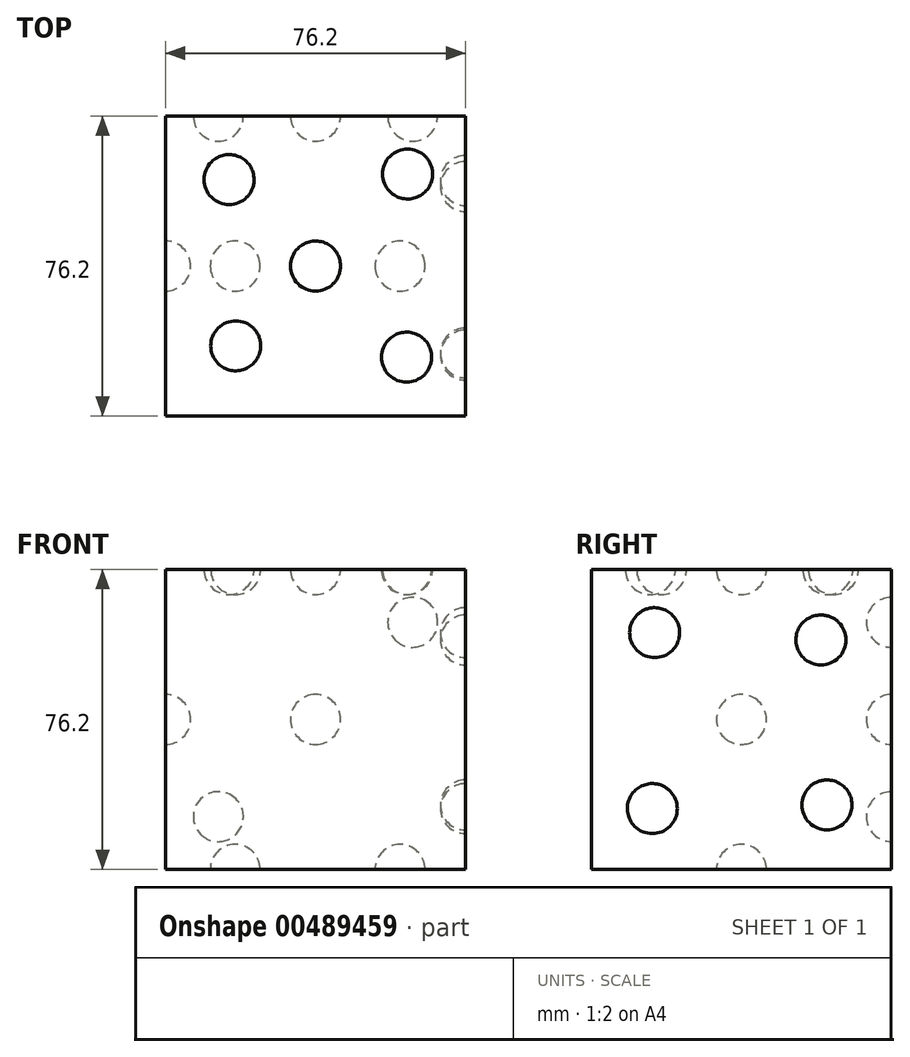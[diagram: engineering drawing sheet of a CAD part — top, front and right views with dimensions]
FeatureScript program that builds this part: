
annotation { "Feature Type Name" : "Feature", "Feature Type Description" : "" }
export const myFeature = defineFeature(function(context is Context, id is Id, definition is map)
    precondition{}
    {
        {
            var Q0;
            Q0=qCreatedBy(makeId("Top.planeOp"),FACE);
            var sketch = newSketch(context, id + "F0", { "sketchPlane" : qUnion([Q0])});
            skLineSegment(sketch, "E0", {"start": v(0, 0) * mm, "end": v(0, 76.2) * mm});
            skLineSegment(sketch, "E1", {"start": v(0, 76.2) * mm, "end": v(-76.2, 76.2) * mm});
            skLineSegment(sketch, "E2", {"start": v(-76.2, 76.2) * mm, "end": v(-76.2, 0) * mm});
            skLineSegment(sketch, "E3", {"start": v(-76.2, 0) * mm, "end": v(0, 0) * mm});
            skSolve(sketch);
        }
        {
            var Q0;
            Q0 = qSketchRegion(id + "F0", true);
            extrude(context, id + "F1", {"entities" : qUnion([Q0]), "depth" : 76.2 * mm});
        }
        {
            var Q0;
            Q0=qCreatedBy(makeId("Front.planeOp"),FACE);
            cPlane(context, id + "F2", {"entities" : qUnion([Q0]), "cplaneType" : CPlaneType.OFFSET, "offset" : 76.2 * mm, "oppositeDirection" : true, "width" : 152.4 * mm, "height" : 152.4 * mm});
        }
        {
            var Q0;
            Q0=qCreatedBy(id+"F2.planeOp",FACE);
            var sketch = newSketch(context, id + "F3", { "sketchPlane" : qUnion([Q0])});
            skPoint(sketch, "E4.trimOffspring.end.orphan", {"position": v(0, 0) * mm});
            skLineSegment(sketch, "E5", {"start": v(-76.2, 76.2) * mm, "end": v(-76.2, 0) * mm});
            skLineSegment(sketch, "E6", {"start": v(-76.2, 0) * mm, "end": v(0, 0) * mm});
            skLineSegment(sketch, "E7", {"start": v(0, 76.2) * mm, "end": v(-76.2, 76.2) * mm});
            skArc(sketch, "E8", {"start": v(-38.1, 31.75) * mm, "mid": v(-31.75, 38.1) * mm, "end": v(-38.1, 44.45) * mm});
            skLineSegment(sketch, "E9", {"start": v(-38.1, 76.2) * mm, "end": v(-38.1, 0) * mm});
            skSolve(sketch);
        }
        {
            var Q0;
            {var subQ0=sQuery(id+"F3.wireOp",EDGE,"E8");Q0=makeQuery(id+"F3.imprint","IMPRINT",FACE,{"disambiguationData":[TD([[makeQuery(id+"F3.imprint","IMPRINT",EDGE,{"derivedFrom":subQ0}),1.0]])]});}
            var Q1;
            Q1=sQuery(id+"F3.wireOp",EDGE,"E9");
            revolve(context, id + "F4", {"operationType" : NewBodyOperationType.REMOVE, "entities" : qUnion([Q0]), "axis" : qUnion([Q1]), "revolveType" : RevolveType.FULL});
        }
        {
            var Q0;
            Q0=makeQuery(id+"F1.opExtrude","SWEPT_FACE",FACE,{"disambiguationData":[OSD([sQuery(id+"F0.wireOp",EDGE,"E2")])]});
            var sketch = newSketch(context, id + "F5", { "sketchPlane" : qUnion([Q0])});
            skLineSegment(sketch, "E10", {"start": v(-76.2, 76.2) * mm, "end": v(0, 0) * mm});
            skArc(sketch, "E11", {"start": v(-42.6, 42.6) * mm, "mid": v(-42.6, 33.6) * mm, "end": v(-33.6, 33.6) * mm});
            skSolve(sketch);
        }
        {
            var Q0;
            {var subQ0=sQuery(id+"F5.wireOp",EDGE,"E11");Q0=makeQuery(id+"F5.imprint","IMPRINT",FACE,{"disambiguationData":[TD([[makeQuery(id+"F5.imprint","IMPRINT",EDGE,{"derivedFrom":subQ0}),1.0]])]});}
            var Q1;
            Q1=sQuery(id+"F5.wireOp",EDGE,"E10");
            revolve(context, id + "F6", {"operationType" : NewBodyOperationType.REMOVE, "entities" : qUnion([Q0]), "axis" : qUnion([Q1]), "revolveType" : RevolveType.FULL, "oppositeDirection" : true});
        }
        {
            var Q0;
            Q0=makeQuery(id+"F1.opExtrude","SWEPT_FACE",FACE,{"disambiguationData":[OSD([sQuery(id+"F0.wireOp",EDGE,"E1")])]});
            var sketch = newSketch(context, id + "F7", { "sketchPlane" : qUnion([Q0])});
            skLineSegment(sketch, "E12", {"start": v(0, 76.2) * mm, "end": v(76.2, 0) * mm});
            skArc(sketch, "E13", {"start": v(17.9, 58.3) * mm, "mid": v(17.9, 67.29) * mm, "end": v(8.91, 67.29) * mm});
            skArc(sketch, "E14", {"start": v(67.29, 8.91) * mm, "mid": v(67.29, 17.9) * mm, "end": v(58.3, 17.9) * mm});
            skSolve(sketch);
        }
        {
            var Q0;
            {var subQ0=sQuery(id+"F7.wireOp",EDGE,"E13");Q0=makeQuery(id+"F7.imprint","IMPRINT",FACE,{"disambiguationData":[TD([[makeQuery(id+"F7.imprint","IMPRINT",EDGE,{"derivedFrom":subQ0}),1.0]])]});}
            var Q1;
            {var subQ0=sQuery(id+"F7.wireOp",EDGE,"E14");Q1=makeQuery(id+"F7.imprint","IMPRINT",FACE,{"disambiguationData":[TD([[makeQuery(id+"F7.imprint","IMPRINT",EDGE,{"derivedFrom":subQ0}),1.0]])]});}
            var Q2;
            Q2=sQuery(id+"F7.wireOp",EDGE,"E12");
            revolve(context, id + "F8", {"operationType" : NewBodyOperationType.REMOVE, "entities" : qUnion([Q0, Q1]), "axis" : qUnion([Q2]), "revolveType" : RevolveType.FULL, "oppositeDirection" : true});
        }
        {
            var Q0;
            Q0=makeQuery(id+"F1.opExtrude","SWEPT_FACE",FACE,{"disambiguationData":[OSD([sQuery(id+"F0.wireOp",EDGE,"E0")])]});
            var sketch = newSketch(context, id + "F9", { "sketchPlane" : qUnion([Q0])});
            skLineSegment(sketch, "E15", {"start": v(0, 76.2) * mm, "end": v(76.2, 0) * mm});
            skArc(sketch, "E16", {"start": v(64.31, 11.89) * mm, "mid": v(64.31, 20.87) * mm, "end": v(55.33, 20.87) * mm});
            skArc(sketch, "E17", {"start": v(20.54, 55.66) * mm, "mid": v(20.54, 64.64) * mm, "end": v(11.56, 64.64) * mm});
            skSolve(sketch);
        }
        {
            var Q0;
            {var subQ0=sQuery(id+"F9.wireOp",EDGE,"E17");Q0=makeQuery(id+"F9.imprint","IMPRINT",FACE,{"disambiguationData":[TD([[makeQuery(id+"F9.imprint","IMPRINT",EDGE,{"derivedFrom":subQ0}),1.0]])]});}
            var Q1;
            {var subQ0=sQuery(id+"F9.wireOp",EDGE,"E16");Q1=makeQuery(id+"F9.imprint","IMPRINT",FACE,{"disambiguationData":[TD([[makeQuery(id+"F9.imprint","IMPRINT",EDGE,{"derivedFrom":subQ0}),1.0]])]});}
            var Q2;
            Q2=sQuery(id+"F9.wireOp",EDGE,"E15");
            revolve(context, id + "F10", {"operationType" : NewBodyOperationType.REMOVE, "entities" : qUnion([Q0, Q1]), "axis" : qUnion([Q2]), "revolveType" : RevolveType.FULL, "oppositeDirection" : true});
        }
        {
            var Q0;
            Q0=makeQuery(id+"F1.opExtrude","SWEPT_FACE",FACE,{"disambiguationData":[OSD([sQuery(id+"F0.wireOp",EDGE,"E0")])]});
            var sketch = newSketch(context, id + "F11", { "sketchPlane" : qUnion([Q0])});
            skLineSegment(sketch, "E18", {"start": v(0, 0) * mm, "end": v(76.2, 76.2) * mm});
            skArc(sketch, "E19", {"start": v(19.95, 19.95) * mm, "mid": v(10.97, 19.95) * mm, "end": v(10.97, 10.97) * mm});
            skArc(sketch, "E20", {"start": v(62.78, 62.78) * mm, "mid": v(53.8, 62.78) * mm, "end": v(53.8, 53.8) * mm});
            skSolve(sketch);
        }
        {
            var Q0;
            {var subQ0=sQuery(id+"F11.wireOp",EDGE,"E19");Q0=makeQuery(id+"F11.imprint","IMPRINT",FACE,{"disambiguationData":[TD([[makeQuery(id+"F11.imprint","IMPRINT",EDGE,{"derivedFrom":subQ0}),1.0]])]});}
            var Q1;
            {var subQ0=sQuery(id+"F11.wireOp",EDGE,"E20");Q1=makeQuery(id+"F11.imprint","IMPRINT",FACE,{"disambiguationData":[TD([[makeQuery(id+"F11.imprint","IMPRINT",EDGE,{"derivedFrom":subQ0}),1.0]])]});}
            var Q2;
            Q2=sQuery(id+"F11.wireOp",EDGE,"E18");
            revolve(context, id + "F12", {"operationType" : NewBodyOperationType.REMOVE, "entities" : qUnion([Q0, Q1]), "axis" : qUnion([Q2]), "revolveType" : RevolveType.FULL, "oppositeDirection" : true});
        }
        {
            var Q0;
            Q0=makeQuery(id+"F1.opExtrude","CAP_FACE",FACE,{"disambiguationData":[OSD([sQuery(id+"F0.wireOp",EDGE,"E0"),sQuery(id+"F0.wireOp",EDGE,"E1"),sQuery(id+"F0.wireOp",EDGE,"E2"),sQuery(id+"F0.wireOp",EDGE,"E3")])],"isStart":true});
            var sketch = newSketch(context, id + "F13", { "sketchPlane" : qUnion([Q0])});
            skLineSegment(sketch, "E21", {"start": v(-76.2, -38.1) * mm, "end": v(0, -38.1) * mm});
            skArc(sketch, "E22", {"start": v(-52.16, -38.1) * mm, "mid": v(-58.51, -31.75) * mm, "end": v(-64.86, -38.1) * mm});
            skArc(sketch, "E23", {"start": v(-10.27, -38.1) * mm, "mid": v(-16.62, -31.75) * mm, "end": v(-22.97, -38.1) * mm});
            skPoint(sketch, "E24.orphan", {"position": v(-38.1, -76.2) * mm});
            skPoint(sketch, "E25.start.orphan", {"position": v(-38.1, 0) * mm});
            skSolve(sketch);
        }
        {
            var Q0;
            {var subQ0=sQuery(id+"F13.wireOp",EDGE,"E22");Q0=makeQuery(id+"F13.imprint","IMPRINT",FACE,{"disambiguationData":[TD([[makeQuery(id+"F13.imprint","IMPRINT",EDGE,{"derivedFrom":subQ0}),1.0]])]});}
            var Q1;
            {var subQ0=sQuery(id+"F13.wireOp",EDGE,"E23");Q1=makeQuery(id+"F13.imprint","IMPRINT",FACE,{"disambiguationData":[TD([[makeQuery(id+"F13.imprint","IMPRINT",EDGE,{"derivedFrom":subQ0}),1.0]])]});}
            var Q2;
            Q2=sQuery(id+"F13.wireOp",EDGE,"E21");
            revolve(context, id + "F14", {"operationType" : NewBodyOperationType.REMOVE, "entities" : qUnion([Q0, Q1]), "axis" : qUnion([Q2]), "revolveType" : RevolveType.FULL, "oppositeDirection" : true});
        }
        {
            var Q0;
            Q0=makeQuery(id+"F1.opExtrude","CAP_FACE",FACE,{"disambiguationData":[OSD([sQuery(id+"F0.wireOp",EDGE,"E0"),sQuery(id+"F0.wireOp",EDGE,"E1"),sQuery(id+"F0.wireOp",EDGE,"E2"),sQuery(id+"F0.wireOp",EDGE,"E3")])],"isStart":false});
            var sketch = newSketch(context, id + "F15", { "sketchPlane" : qUnion([Q0])});
            skLineSegment(sketch, "E26", {"start": v(-76.2, 76.2) * mm, "end": v(0, 0) * mm});
            skArc(sketch, "E27", {"start": v(-33.6, 33.6) * mm, "mid": v(-33.6, 42.6) * mm, "end": v(-42.6, 42.6) * mm});
            skArc(sketch, "E28", {"start": v(-55.57, 55.57) * mm, "mid": v(-55.57, 64.55) * mm, "end": v(-64.55, 64.55) * mm});
            skArc(sketch, "E29", {"start": v(-10.47, 10.47) * mm, "mid": v(-10.47, 19.45) * mm, "end": v(-19.45, 19.45) * mm});
            skSolve(sketch);
        }
        {
            var Q0;
            {var subQ0=sQuery(id+"F15.wireOp",EDGE,"E28");Q0=makeQuery(id+"F15.imprint","IMPRINT",FACE,{"disambiguationData":[TD([[makeQuery(id+"F15.imprint","IMPRINT",EDGE,{"derivedFrom":subQ0}),1.0]])]});}
            var Q1;
            {var subQ0=sQuery(id+"F15.wireOp",EDGE,"E27");Q1=makeQuery(id+"F15.imprint","IMPRINT",FACE,{"disambiguationData":[TD([[makeQuery(id+"F15.imprint","IMPRINT",EDGE,{"derivedFrom":subQ0}),1.0]])]});}
            var Q2;
            {var subQ0=sQuery(id+"F15.wireOp",EDGE,"E29");Q2=makeQuery(id+"F15.imprint","IMPRINT",FACE,{"disambiguationData":[TD([[makeQuery(id+"F15.imprint","IMPRINT",EDGE,{"derivedFrom":subQ0}),1.0]])]});}
            var Q3;
            Q3=sQuery(id+"F15.wireOp",EDGE,"E26");
            revolve(context, id + "F16", {"operationType" : NewBodyOperationType.REMOVE, "entities" : qUnion([Q0, Q1, Q2]), "axis" : qUnion([Q3]), "revolveType" : RevolveType.FULL, "oppositeDirection" : true});
        }
        {
            var Q0;
            Q0=makeQuery(id+"F1.opExtrude","CAP_FACE",FACE,{"disambiguationData":[OSD([sQuery(id+"F0.wireOp",EDGE,"E0"),sQuery(id+"F0.wireOp",EDGE,"E1"),sQuery(id+"F0.wireOp",EDGE,"E2"),sQuery(id+"F0.wireOp",EDGE,"E3")])],"isStart":false});
            var sketch = newSketch(context, id + "F17", { "sketchPlane" : qUnion([Q0])});
            skLineSegment(sketch, "E30", {"start": v(-76.2, 0) * mm, "end": v(0, 76.2) * mm});
            skArc(sketch, "E31", {"start": v(-53.89, 22.31) * mm, "mid": v(-62.87, 22.31) * mm, "end": v(-62.87, 13.33) * mm});
            skArc(sketch, "E32", {"start": v(-10.23, 65.97) * mm, "mid": v(-19.2, 65.97) * mm, "end": v(-19.2, 57) * mm});
            skSolve(sketch);
        }
        {
            var Q0;
            {var subQ0=sQuery(id+"F17.wireOp",EDGE,"E31");Q0=makeQuery(id+"F17.imprint","IMPRINT",FACE,{"disambiguationData":[TD([[makeQuery(id+"F17.imprint","IMPRINT",EDGE,{"derivedFrom":subQ0}),1.0]])]});}
            var Q1;
            {var subQ0=sQuery(id+"F17.wireOp",EDGE,"E32");Q1=makeQuery(id+"F17.imprint","IMPRINT",FACE,{"disambiguationData":[TD([[makeQuery(id+"F17.imprint","IMPRINT",EDGE,{"derivedFrom":subQ0}),1.0]])]});}
            var Q2;
            Q2=sQuery(id+"F17.wireOp",EDGE,"E30");
            revolve(context, id + "F18", {"operationType" : NewBodyOperationType.REMOVE, "entities" : qUnion([Q0, Q1]), "axis" : qUnion([Q2]), "revolveType" : RevolveType.FULL, "oppositeDirection" : true});
        }
    });
